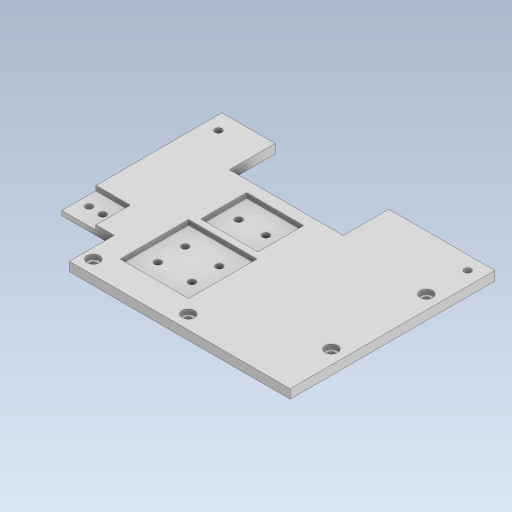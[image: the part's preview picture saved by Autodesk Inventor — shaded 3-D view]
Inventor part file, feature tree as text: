
AUTODESK INVENTOR PART (.ipt)
format: ipt  version: 2023.5 (Build 275446000, 446)  size: 383,488 bytes
history: native  units: in
note: dims shown in document units (in); Inventor stores cm internally (conversion verified against a paired STEP export)
features: extrude x2, sketch x1
ambient origin geometry x8: Origin, YZ Plane, XZ Plane, XY Plane, X Axis, Y Axis, Z Axis, Center Point
bodies: Solid1 (feature_tree)
feature tree (3):
  sketch  "Sketch1"  dims[d28=0.1575in d29=0.0in d30=0.0787in d31=0.0in d32=0.4724in d33=0.2953in d34=0.2953in d35=0.4724in d36=0.0in d37=0.0in d39=0.315in d40=0.2165in d41=0.2165in d42=0.2165in d43=0.2165in]
  extrude  "Extrusion1"  Depth=0.0787in TaperAngle=0.0deg
  extrude  "Extrusion2"  Depth=0.4724in
